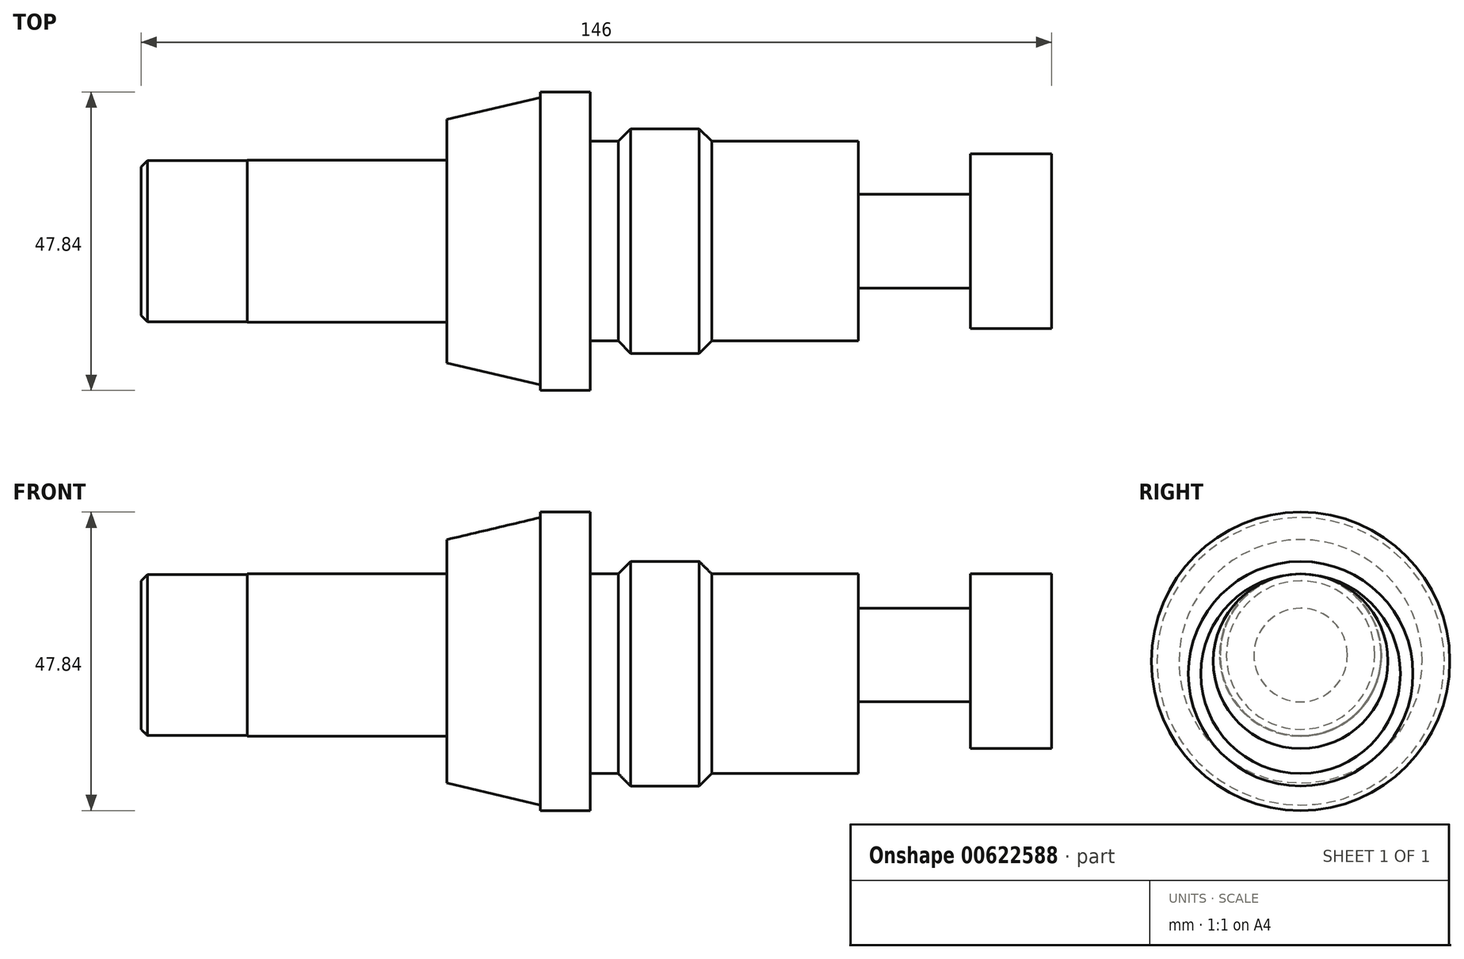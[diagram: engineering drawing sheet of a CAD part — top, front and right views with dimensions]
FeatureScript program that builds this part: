
annotation { "Feature Type Name" : "Feature", "Feature Type Description" : "" }
export const myFeature = defineFeature(function(context is Context, id is Id, definition is map)
    precondition{}
    {
        {
            var Q0;
            Q0=qCreatedBy(makeId("Front.planeOp"),FACE);
            var sketch = newSketch(context, id + "F0", { "sketchPlane" : qUnion([Q0])});
            skLineSegment(sketch, "E0", {"start": v(0, 0) * mm, "end": v(0, 19.5) * mm});
            skLineSegment(sketch, "E1", {"start": v(0, 19.5) * mm, "end": v(15, 23.05) * mm});
            skLineSegment(sketch, "E2", {"start": v(15, 23.05) * mm, "end": v(15, 23.92) * mm});
            skLineSegment(sketch, "E3", {"start": v(15, 23.92) * mm, "end": v(23, 23.92) * mm});
            skLineSegment(sketch, "E4", {"start": v(23, 23.92) * mm, "end": v(23, 0) * mm});
            skLineSegment(sketch, "E5", {"start": v(23, 0) * mm, "end": v(0, 0) * mm});
            skLineSegment(sketch, "E6", {"start": v(-4.06, 0) * mm, "end": v(26.23, 0) * mm, "construction": true});
            skSolve(sketch);
        }
        {
            var Q0;
            Q0=makeQuery(id+"F0.imprint","IMPRINT",FACE,{"disambiguationData":[TD([[makeQuery(id+"F0.imprint","IMPRINT",EDGE,{"derivedFrom":sQuery(id+"F0.wireOp",EDGE,"E0")}),-1.0]])]});
            var Q1;
            Q1=sQuery(id+"F0.wireOp",EDGE,"E6");
            revolve(context, id + "F1", {"entities" : qUnion([Q0]), "axis" : qUnion([Q1]), "revolveType" : RevolveType.FULL});
        }
        {
            var Q0;
            Q0=qCreatedBy(makeId("Front.planeOp"),FACE);
            var sketch = newSketch(context, id + "F2", { "sketchPlane" : qUnion([Q0])});
            skLineSegment(sketch, "E7", {"start": v(44.58, -2) * mm, "end": v(65.32, -2) * mm, "construction": true});
            skLineSegment(sketch, "E8", {"start": v(23, 14) * mm, "end": v(27, 14) * mm});
            skLineSegment(sketch, "E9", {"start": v(27, 14) * mm, "end": v(27, 16) * mm});
            skLineSegment(sketch, "E10", {"start": v(27, 16) * mm, "end": v(43, 16) * mm});
            skLineSegment(sketch, "E11", {"start": v(43, 16) * mm, "end": v(43, 14) * mm});
            skLineSegment(sketch, "E12", {"start": v(43, 14) * mm, "end": v(66, 14) * mm});
            skLineSegment(sketch, "E13", {"start": v(66, 14) * mm, "end": v(66, -2) * mm});
            skLineSegment(sketch, "E14", {"start": v(66, -2) * mm, "end": v(23, -2) * mm});
            skLineSegment(sketch, "E15", {"start": v(23, -2) * mm, "end": v(23, 14) * mm});
            skSolve(sketch);
        }
        {
            var Q0;
            Q0=makeQuery(id+"F2.imprint","IMPRINT",FACE,{"disambiguationData":[TD([[makeQuery(id+"F2.imprint","IMPRINT",EDGE,{"derivedFrom":sQuery(id+"F2.wireOp",EDGE,"E8")}),-1.0]])]});
            var Q1;
            Q1=sQuery(id+"F2.wireOp",EDGE,"E14");
            revolve(context, id + "F3", {"operationType" : NewBodyOperationType.ADD, "entities" : qUnion([Q0]), "axis" : qUnion([Q1]), "revolveType" : RevolveType.FULL});
        }
        {
            var Q0;
            Q0=makeQuery(id+"F3.opRevolve","SWEPT_EDGE",EDGE,{"disambiguationData":[OSD([sQuery(id+"F2.wireOp",EDGE,"E9"),sQuery(id+"F2.wireOp",EDGE,"E10")])]});
            var Q1;
            Q1=makeQuery(id+"F3.opRevolve","SWEPT_EDGE",EDGE,{"disambiguationData":[OSD([sQuery(id+"F2.wireOp",EDGE,"E10"),sQuery(id+"F2.wireOp",EDGE,"E11")])]});
            chamfer(context, id + "F4", {"entities" : qUnion([Q0, Q1]), "width" : 2.5 * mm, "tangentPropagation" : true});
        }
        {
            var Q0;
            Q0=makeQuery(id+"F3.opRevolve","SWEPT_FACE",FACE,{"disambiguationData":[OSD([sQuery(id+"F2.wireOp",EDGE,"E13")])]});
            var sketch = newSketch(context, id + "F5", { "sketchPlane" : qUnion([Q0])});
            skCircle(sketch, "E16", {"center": v(0, 1) * mm, "radius": 7.5 * mm});
            skSolve(sketch);
        }
        {
            var Q0;
            Q0 = qSketchRegion(id + "F5", true);
            extrude(context, id + "F6", {"entities" : qUnion([Q0]), "operationType" : NewBodyOperationType.ADD, "depth" : 18 * mm, "offsetDistance" : 25 * mm});
        }
        {
            var Q0;
            Q0=makeQuery(id+"F6.opExtrude","CAP_FACE",FACE,{"disambiguationData":[OSD([sQuery(id+"F5.wireOp",EDGE,"E16")])],"isStart":false});
            var sketch = newSketch(context, id + "F7", { "sketchPlane" : qUnion([Q0])});
            skCircle(sketch, "E17", {"center": v(0, 0) * mm, "radius": 14 * mm});
            skSolve(sketch);
        }
        {
            var Q0;
            Q0 = qSketchRegion(id + "F7", true);
            extrude(context, id + "F8", {"entities" : qUnion([Q0]), "operationType" : NewBodyOperationType.ADD, "depth" : 13 * mm, "offsetDistance" : 25 * mm});
        }
        {
            var Q0;
            Q0=makeQuery(id+"F8.opExtrude","CAP_FACE",FACE,{"disambiguationData":[OSD([sQuery(id+"F7.wireOp",EDGE,"E17")])],"isStart":false});
            cPlane(context, id + "F9", {"entities" : qUnion([Q0]), "cplaneType" : CPlaneType.OFFSET, "offset" : 146 * mm, "oppositeDirection" : true, "width" : 150 * mm, "height" : 150 * mm});
        }
        {
            var Q0;
            Q0=qCreatedBy(id+"F9.planeOp",FACE);
            cPlane(context, id + "F10", {"entities" : qUnion([Q0]), "cplaneType" : CPlaneType.OFFSET, "offset" : 17 * mm, "width" : 150 * mm, "height" : 150 * mm});
        }
        {
            var Q0;
            Q0=makeQuery(id+"F1.opRevolve","SWEPT_FACE",FACE,{"disambiguationData":[OSD([sQuery(id+"F0.wireOp",EDGE,"E0")])]});
            var sketch = newSketch(context, id + "F11", { "sketchPlane" : qUnion([Q0])});
            skCircle(sketch, "E18", {"center": v(0, 1) * mm, "radius": 13 * mm});
            skSolve(sketch);
        }
        {
            var Q0;
            Q0 = qSketchRegion(id + "F11", true);
            var Q1;
            Q1=qCreatedBy(id+"F10.planeOp",FACE);
            extrude(context, id + "F12", {"entities" : qUnion([Q0]), "operationType" : NewBodyOperationType.ADD, "endBound" : BoundingType.UP_TO_SURFACE, "depth" : 25 * mm, "endBoundEntityFace" : qUnion([Q1]), "offsetDistance" : 25 * mm});
        }
        {
            var Q0;
            Q0=makeQuery(id+"F12.opExtrude","CAP_FACE",FACE,{"disambiguationData":[OSD([sQuery(id+"F11.wireOp",EDGE,"E18")])],"isStart":false});
            var sketch = newSketch(context, id + "F13", { "sketchPlane" : qUnion([Q0])});
            skCircle(sketch, "E19", {"center": v(0, 1) * mm, "radius": 12.9 * mm});
            skSolve(sketch);
        }
        {
            var Q0;
            Q0=makeQuery(id+"F13.imprint","IMPRINT",FACE,{"disambiguationData":[TD([[makeQuery(id+"F13.imprint","IMPRINT",EDGE,{"derivedFrom":sQuery(id+"F13.wireOp",EDGE,"E19")}),1.0]])]});
            var Q1;
            Q1=qCreatedBy(id+"F9.planeOp",FACE);
            extrude(context, id + "F14", {"entities" : qUnion([Q0]), "operationType" : NewBodyOperationType.ADD, "endBound" : BoundingType.UP_TO_SURFACE, "depth" : 25 * mm, "endBoundEntityFace" : qUnion([Q1]), "offsetDistance" : 25 * mm});
        }
        {
            var Q0;
            Q0=makeQuery(id+"F14.opExtrude","CAP_EDGE",EDGE,{"disambiguationData":[OSD([sQuery(id+"F13.wireOp",EDGE,"E19")])],"isStart":false});
            chamfer(context, id + "F15", {"entities" : qUnion([Q0]), "width" : 1 * mm, "tangentPropagation" : true});
        }
    });
